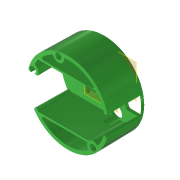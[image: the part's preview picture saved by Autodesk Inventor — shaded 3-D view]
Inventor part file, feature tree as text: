
AUTODESK INVENTOR PART (.ipt)
format: ipt  version: 2022 (Build 260153000, 153)  size: 616,960 bytes
history: native  units: in
note: dims shown in document units (in); Inventor stores cm internally (conversion verified against a paired STEP export)
features: extrude x13, sketch x13, plane x5, other x5, reference x4, projected_geometry x2, fillet x1
ambient origin geometry x8: Origin, YZ Plane, XZ Plane, XY Plane, X Axis, Y Axis, Z Axis, Center Point
bodies: Solid1 (feature_tree)
feature tree (43):
  plane  "Arbeitsebene6"
  extrude  "Extrusion1"  Depth=0.0787in
  extrude  "Extrusion2"  Depth=1.0in
  plane  "Arbeitsebene3"
  extrude  "Extrusion6"  Depth=0.1102in
  plane  "Arbeitsebene2"
  extrude  "Extrusion7"  Depth=0.0787in
  extrude  "Extrusion10"  Depth=0.0394in TaperAngle=0.0deg
  plane  "Arbeitsebene7"
  sketch  "Skizze16"  dims[d81=0.0591in d82=0.3937in d83=0.0069in]
  plane  "Arbeitsebene5"
  extrude  "Extrusion14"  Depth=0.3937in
  extrude  "Extrusion15"  Depth=0.0787in
  extrude  "Extrusion17"  TaperAngle=0.0deg  [1 undecoded]
  extrude  "Extrusion18"  Depth=0.1575in
  extrude  "Extrusion19"  Depth=0.1575in
  extrude  "Extrusion20"  Depth=0.8465in TaperAngle=0.0deg
  fillet  "Rundung2"  Radius=0.1614in
  extrude  "Extrusion21"  Depth=0.1614in
  extrude  "Extrusion22"  Depth=0.0394in
  sketch  "Sketch1"  dims[d0=0.0787in d1=-0.0069in d2=0.315in]
  sketch  "Sketch2"  dims[d3=0.3189in d4=1.0in d5=-0.0137in]
  sketch  "Sketch8"  dims[d33=0.1102in d34=0.1102in]
  sketch  "Sketch9"  dims[d35=0.0in d36=0.0in d37=0.0787in]
  sketch  "Skizze12"  dims[d38=0.0004in d39=-0.0069in d51=0.0394in d52=0.0in]
  sketch  "Skizze17"  dims[d89=0.3937in d90=-0.0069in d91=0.0787in]
  reference  "Referenz44"
  reference  "Referenz45"
  projected_geometry  "Projizierte Kontur4"
  sketch  "Skizze19"  dims[d92=0.0787in d93=0.0in]
  sketch  "Skizze20"  dims[d94=0.0in d104=0.1575in]
  sketch  "Skizze21"  dims[d105=0.1575in d106=0.1575in]
  sketch  "Skizze22"  dims[d107=0.0001in d108=-0.0069in d109=0.8465in d110=0.0in d111=0.1614in]
  reference  "Referenz46"
  sketch  "Skizze23"  dims[d112=0.1614in d113=0.1614in]
  sketch  "Skizze24"  dims[d114=0.1969in d115=-0.0069in d116=0.315in d117=0.315in d118=0.0069in d119=0.0394in d120=0.0394in d122=0.9055in d123=0.4528in d124=1.8701in d125=0.2756in d126=0.4724in d127=0.5906in d128=0.0394in d129=0.0in d130=0.315in d131=0.315in d132=0.1102in d133=0.1102in d134=0.0in d135=0.0in d78=0.0197in d79=0.0344in d80=0.0197in d95=0.0197in d96=0.0344in d97=0.0197in d98=0.0344in]
  projected_geometry  "Projizierte Kontur5"
  reference  "Referenz47"
  other  "Matchboxscope_VCM_v1.iam"
  other  "Matchboxscope_bottom_v0:2"
  other  "Matchboxscope_middle2_m12VCMLens_v2:2"
  other  "Assembly_Matchboxscope_injectionmolded.iam"
  other  "IM_Matchboxscope_plate:1"
note: 1 required parameter value undecoded (feature->parameter linkage not recoverable at this tier; creation-order binding heuristic only, values carry confidence <= 0.55)
